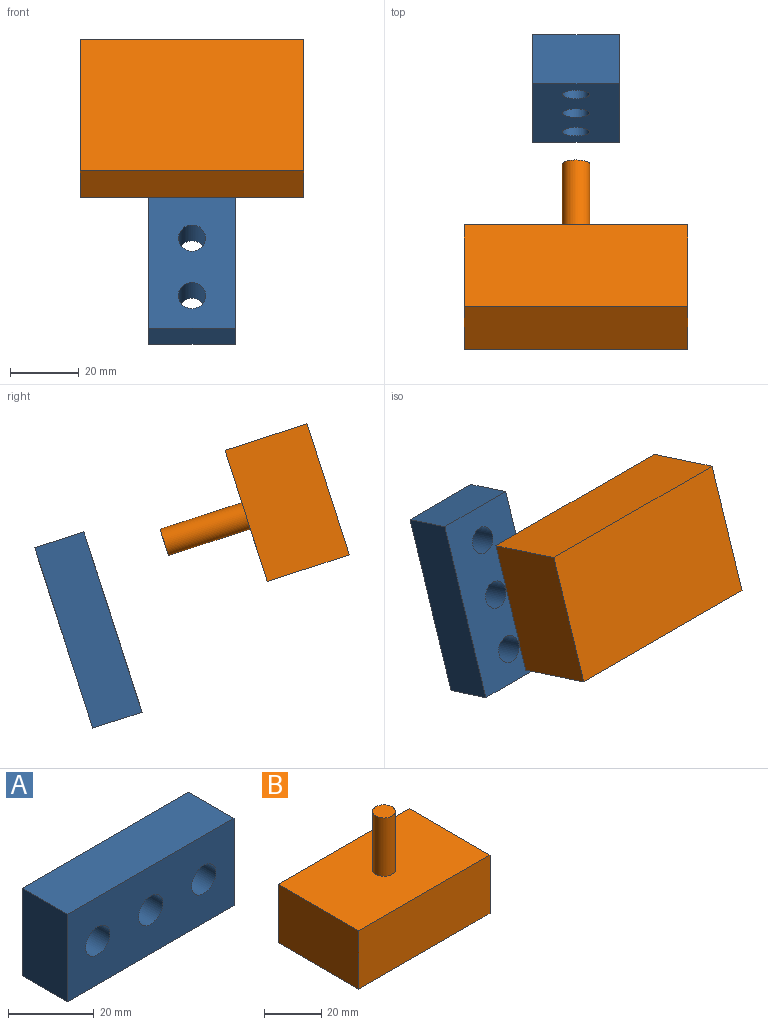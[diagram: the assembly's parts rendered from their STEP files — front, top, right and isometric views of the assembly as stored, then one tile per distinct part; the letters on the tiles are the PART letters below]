
ASSEMBLY  parts=2 mates=1
PART A: 9 faces, bbox 55x15x25 mm
  f0: plane 25x15mm, normal (1,0,0), area 375mm2, adj f1,f3,f4,f5
  f1: plane 55x25mm, normal (0,1,0), area 1224.2mm2, adj f0,f2,f4,f5,f6,f7,f8
  f2: plane 25x15mm, normal (-1,0,0), area 375mm2, adj f1,f3,f4,f5
  f3: plane 55x25mm, normal (0,-1,0), area 1224.2mm2, adj f0,f2,f4,f5,f6,f7,f8
  f4: plane 55x15mm, normal (0,0,1), area 825mm2, adj f0,f1,f2,f3
  f5: plane 55x15mm, normal (0,0,-1), area 825mm2, adj f0,f1,f2,f3
  f6: cylinder r=4mm len=15mm, axis (0,-1,0), area 377mm2, adj f1,f3
  f7: cylinder r=4mm len=15mm, axis (0,-1,0), area 377mm2, adj f1,f3
  f8: cylinder r=4mm len=15mm, axis (0,-1,0), area 377mm2, adj f1,f3
PART B: 8 faces, bbox 65x40x50 mm
  f0: plane 40x25mm, normal (1,0,0), area 1000mm2, adj f1,f3,f4,f5
  f1: plane 65x25mm, normal (0,1,0), area 1625mm2, adj f0,f2,f4,f5
  f2: plane 40x25mm, normal (-1,0,0), area 1000mm2, adj f1,f3,f4,f5
  f3: plane 65x25mm, normal (0,-1,0), area 1625mm2, adj f0,f2,f4,f5
  f4: plane 65x40mm, normal (0,0,1), area 2549.7mm2, adj f0,f1,f2,f3,f6
  f5: plane 65x40mm, normal (0,0,-1), area 2600mm2, adj f0,f1,f2,f3
  f6: cylinder r=4mm len=25mm, axis (0,0,-1), area 628.3mm2, adj f4,f7
  f7: plane 8x8mm, normal (0,0,1), area 50.3mm2, adj f6
PLACE A rot(axis=(-0.15,0.98,-0.15),91.4deg) t=(-32.04,-33.36,39.41)mm
PLACE B rot(axis=(0,0.81,0.59),180deg) t=(-72.55,-68.84,76.52)mm
MATE cylindrical B.f6 <-> A.f7  axis (0,-0.95,0.31) through (-19.54,-26.84,84.59)mm
